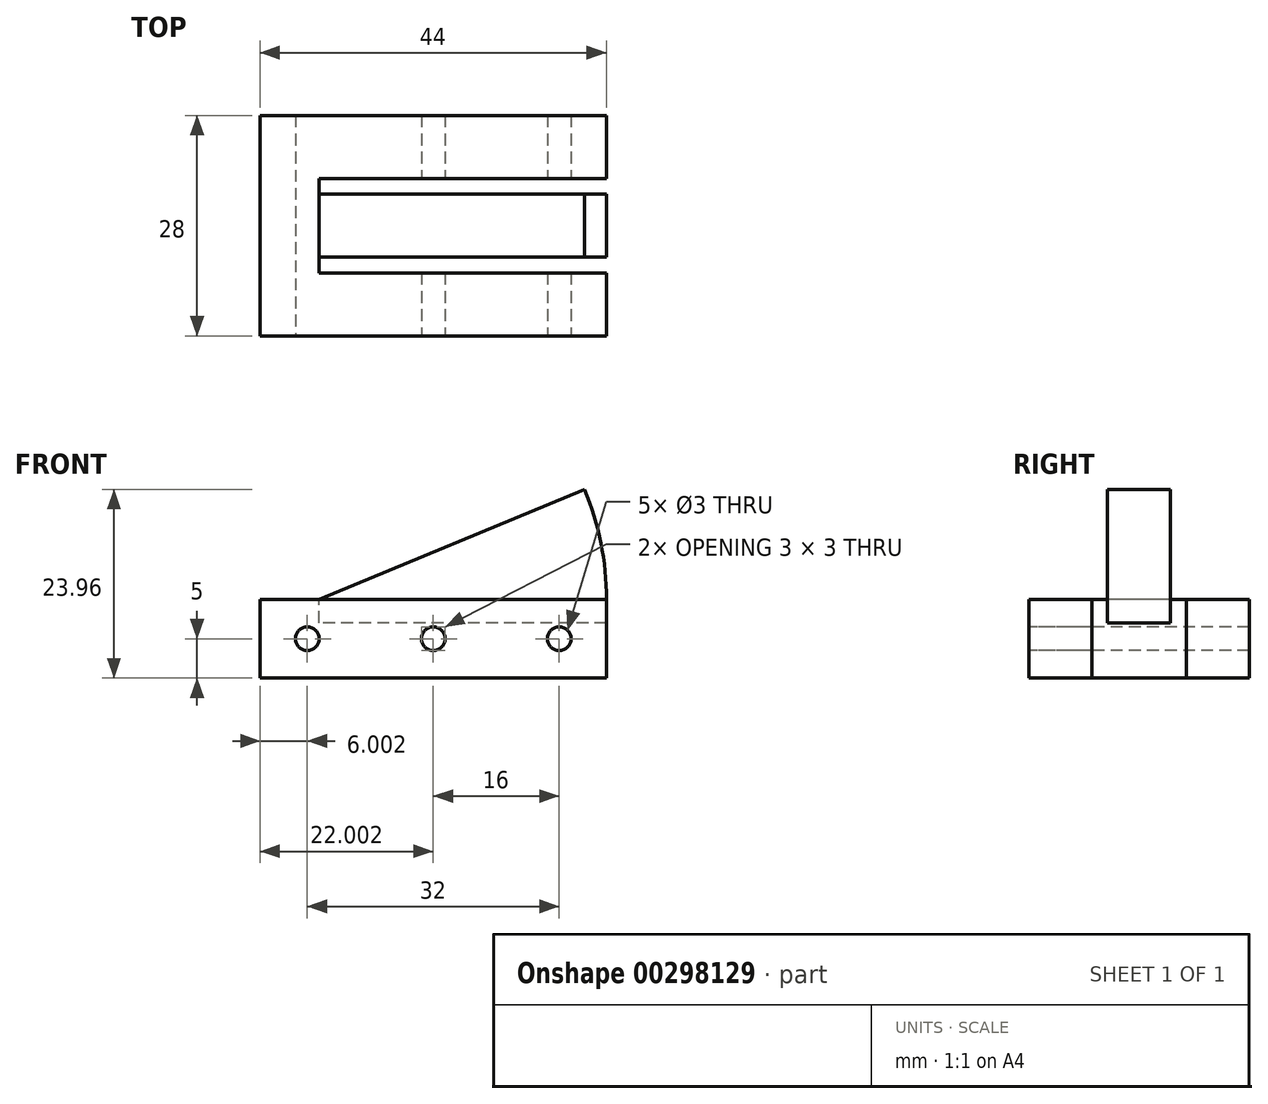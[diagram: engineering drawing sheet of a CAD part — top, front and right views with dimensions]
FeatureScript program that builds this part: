
annotation { "Feature Type Name" : "Feature", "Feature Type Description" : "" }
export const myFeature = defineFeature(function(context is Context, id is Id, definition is map)
    precondition{}
    {
        {
            var Q0;
            Q0=qCreatedBy(makeId("Top.planeOp"),FACE);
            var sketch = newSketch(context, id + "F0", { "sketchPlane" : qUnion([Q0])});
            skLineSegment(sketch, "E0.bottom", {"start": v(-17.49, 10) * mm, "end": v(26.51, 10) * mm});
            skLineSegment(sketch, "E0.top", {"start": v(-17.49, -18) * mm, "end": v(26.51, -18) * mm});
            skLineSegment(sketch, "E0.left", {"start": v(-17.49, 10) * mm, "end": v(-17.49, -18) * mm});
            skLineSegment(sketch, "E0.right", {"start": v(26.51, 10) * mm, "end": v(26.51, -18) * mm});
            skLineSegment(sketch, "E1.bottom", {"start": v(26.51, 2) * mm, "end": v(-9.98, 2) * mm});
            skLineSegment(sketch, "E1.top", {"start": v(26.51, -10) * mm, "end": v(-9.98, -10) * mm});
            skLineSegment(sketch, "E1.left", {"start": v(26.51, 2) * mm, "end": v(26.51, -10) * mm});
            skLineSegment(sketch, "E1.right", {"start": v(-9.98, 2) * mm, "end": v(-9.98, -10) * mm});
            skLineSegment(sketch, "E2.bottom", {"start": v(26.51, -8) * mm, "end": v(-9.98, -8) * mm});
            skLineSegment(sketch, "E2.top", {"start": v(26.51, 0) * mm, "end": v(-9.98, 0) * mm});
            skLineSegment(sketch, "E2.left", {"start": v(26.51, -8) * mm, "end": v(26.51, 0) * mm});
            skLineSegment(sketch, "E2.right", {"start": v(-9.98, -8) * mm, "end": v(-9.98, 0) * mm});
            skSolve(sketch);
        }
        {
            var Q0;
            {var subQ1=sQuery(id+"F0.wireOp",EDGE,"E0.bottom");Q0=makeQuery(id+"F0.imprint","IMPRINT",FACE,{"disambiguationData":[TD([[makeQuery(id+"F0.imprint","IMPRINT",EDGE,{"derivedFrom":subQ1}),-1.0]])]});}
            extrude(context, id + "F1", {"entities" : qUnion([Q0]), "oppositeDirection" : true, "depth" : 10 * mm});
        }
        {
            var Q0;
            Q0=makeQuery(id+"F0.imprint","IMPRINT",FACE,{"disambiguationData":[TD([[makeQuery(id+"F0.imprint","IMPRINT",EDGE,{"derivedFrom":sQuery(id+"F0.wireOp",EDGE,"E2.bottom")}),-1.0]])]});
            extrude(context, id + "F2", {"entities" : qUnion([Q0]), "operationType" : NewBodyOperationType.ADD, "oppositeDirection" : true, "depth" : 3 * mm});
        }
        {
            var Q0;
            Q0=makeQuery(id+"F0.imprint","IMPRINT",FACE,{"disambiguationData":[TD([[makeQuery(id+"F0.imprint","IMPRINT",EDGE,{"derivedFrom":sQuery(id+"F0.wireOp",EDGE,"E2.bottom")}),-1.0]])]});
            var Q1;
            Q1=sQuery(id+"F0.wireOp",EDGE,"E2.right");
            revolve(context, id + "F3", {"operationType" : NewBodyOperationType.ADD, "entities" : qUnion([Q0]), "axis" : qUnion([Q1]), "revolveType" : RevolveType.ONE_DIRECTION, "oppositeDirection" : true, "angle" : 22.5 * degree});
        }
        {
            var Q0;
            Q0=makeQuery(id+"F1.opExtrude","SWEPT_FACE",FACE,{"disambiguationData":[OSD([sQuery(id+"F0.wireOp",EDGE,"E0.top")])]});
            var sketch = newSketch(context, id + "F4", { "sketchPlane" : qUnion([Q0])});
            skCircle(sketch, "E3", {"center": v(20.51, -5) * mm, "radius": 1.5 * mm});
            skCircle(sketch, "E4.1.0.0", {"center": v(4.51, -5) * mm, "radius": 1.5 * mm});
            skCircle(sketch, "E4.2.0.0", {"center": v(-11.49, -5) * mm, "radius": 1.5 * mm});
            skLineSegment(sketch, "E4.direction1", {"start": v(20.51, -5) * mm, "end": v(4.51, -5) * mm, "construction": true});
            skSolve(sketch);
        }
        {
            var Q0;
            Q0=makeQuery(id+"F4.imprint","IMPRINT",FACE,{"disambiguationData":[TD([[makeQuery(id+"F4.imprint","IMPRINT",EDGE,{"derivedFrom":sQuery(id+"F4.wireOp",EDGE,"E4.2.0.0")}),1.0]])]});
            var Q1;
            Q1=makeQuery(id+"F4.imprint","IMPRINT",FACE,{"disambiguationData":[TD([[makeQuery(id+"F4.imprint","IMPRINT",EDGE,{"derivedFrom":sQuery(id+"F4.wireOp",EDGE,"E4.1.0.0")}),1.0]])]});
            var Q2;
            Q2=makeQuery(id+"F4.imprint","IMPRINT",FACE,{"disambiguationData":[TD([[makeQuery(id+"F4.imprint","IMPRINT",EDGE,{"derivedFrom":sQuery(id+"F4.wireOp",EDGE,"E3")}),1.0]])]});
            extrude(context, id + "F5", {"entities" : qUnion([Q0, Q1, Q2]), "operationType" : NewBodyOperationType.REMOVE, "endBound" : BoundingType.THROUGH_ALL, "oppositeDirection" : true, "depth" : 25 * mm});
        }
    });
